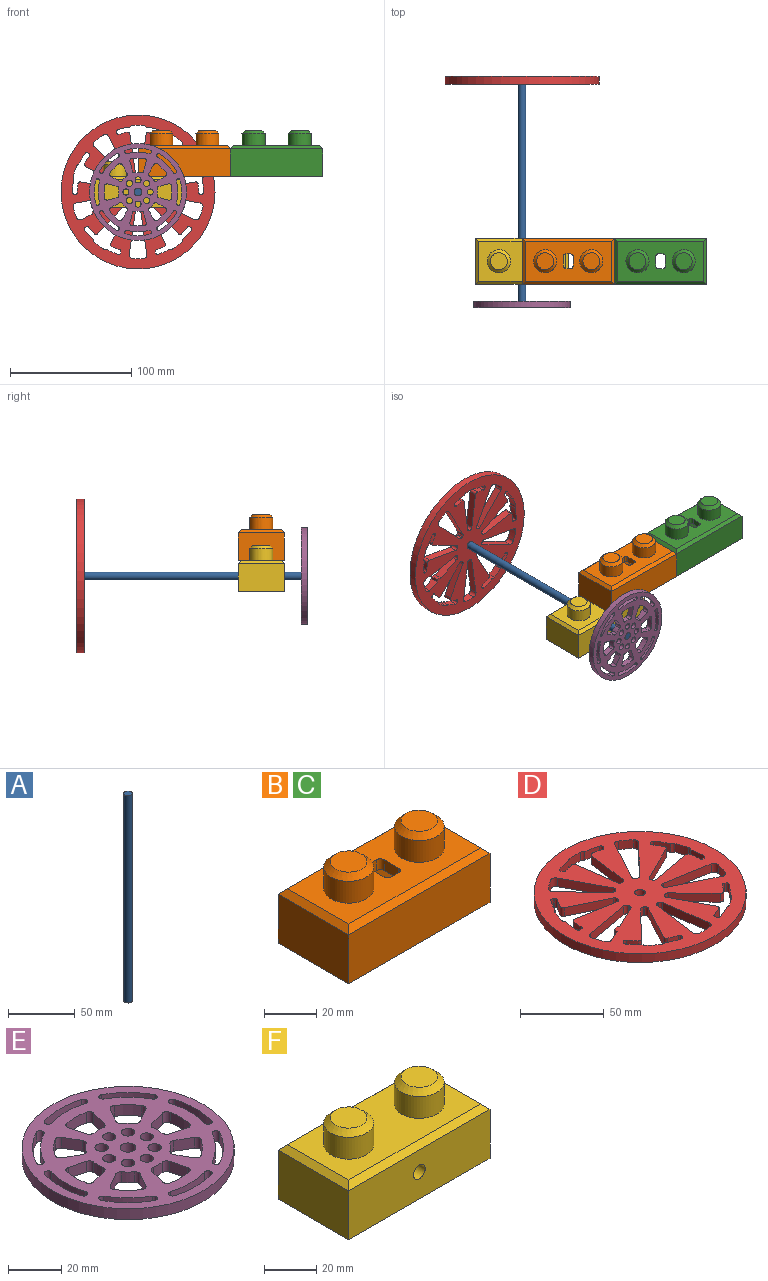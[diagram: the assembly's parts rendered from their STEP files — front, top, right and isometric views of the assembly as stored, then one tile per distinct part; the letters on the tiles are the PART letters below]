
ASSEMBLY  parts=6 mates=5
PART A: 3 faces, bbox 6.4x6.4x190.5 mm
  f0: cylinder r=3.17mm len=190.5mm, axis (0,0,-1), area 3800.3mm2, adj f1,f2
  f1: plane 6.35x6.35mm, normal (0,0,1), area 31.7mm2, adj f0
  f2: plane 6.35x6.35mm, normal (0,0,-1), area 31.7mm2, adj f0
PART B: 33 faces, bbox 76.2x38.1x38.1 mm
  f0: plane 71.12x33.02mm, normal (0,0,1), area 1685.8mm2, adj f7,f9,f13,f14,f15,f16,f25,f26
  f1: plane 66.04x27.94mm, normal (0,0,-1), area 1628.4mm2, adj f19,f20,f21,f22,f23,f24,f25,f26
  f2: plane 76.2x38.1mm, normal (0,0,-1), area 1058.1mm2, adj f3,f4,f5,f6,f19,f20,f21,f22
  f3: plane 76.2x22.86mm, normal (0,1,0), area 1741.9mm2, adj f2,f4,f6,f16
  f4: plane 38.1x22.86mm, normal (-1,0,0), area 871mm2, adj f2,f3,f5,f14
  f5: plane 76.2x22.86mm, normal (0,-1,0), area 1741.9mm2, adj f2,f4,f6,f13
  f6: plane 38.1x22.86mm, normal (1,0,0), area 871mm2, adj f2,f3,f5,f15
  f7: cylinder r=9.53mm len=19.05mm, axis (0,0,-1), area 608mm2, adj f0,f12
  f8: plane 13.97x13.97mm, normal (0,0,1), area 153.3mm2, adj f12
  f9: cylinder r=9.53mm len=19.05mm, axis (0,0,-1), area 608mm2, adj f0,f11
  f10: plane 13.97x13.97mm, normal (0,0,1), area 153.3mm2, adj f11
  f11: cone r=6.99mm half-angle=45deg, axis (0,0,-1), area 186.3mm2, adj f9,f10
  f12: cone r=6.99mm half-angle=45deg, axis (0,0,-1), area 186.3mm2, adj f7,f8
  f13: plane 76.2x2.54mm, normal (0,-0.71,0.71), area 264.6mm2, adj f0,f5,f14,f15
  f14: plane 38.1x2.54mm, normal (-0.71,0,0.71), area 127.7mm2, adj f0,f4,f13,f16
  f15: plane 38.1x2.54mm, normal (0.71,0,0.71), area 127.7mm2, adj f0,f6,f13,f16
  f16: plane 76.2x2.54mm, normal (0,0.71,0.71), area 264.6mm2, adj f0,f3,f14,f15
  f17: plane 8.89x8.89mm, normal (0,0,-1), area 62.1mm2, adj f24
  f18: plane 8.89x8.89mm, normal (0,0,-1), area 62.1mm2, adj f23
  f19: plane 66.04x20.32mm, normal (0,-1,0), area 1341.9mm2, adj f1,f2,f20,f22
  f20: plane 27.94x20.32mm, normal (1,0,0), area 567.7mm2, adj f1,f2,f19,f21
  f21: plane 66.04x20.32mm, normal (0,1,0), area 1341.9mm2, adj f1,f2,f20,f22
  f22: plane 27.94x20.32mm, normal (-1,0,0), area 567.7mm2, adj f1,f2,f19,f21
  f23: cylinder r=4.45mm len=12.7mm, axis (0,0,-1), area 354.7mm2, adj f1,f18
  f24: cylinder r=4.45mm len=12.7mm, axis (0,0,-1), area 354.7mm2, adj f1,f17
  f25: plane 5.08x4mm, normal (0,-1,0), area 20.3mm2, adj f0,f1,f26,f32
  f26: cylinder r=2mm len=5.08mm, axis (0,0,1), area 16mm2, adj f0,f1,f25,f27
  f27: plane 8x5.08mm, normal (1,0,0), area 40.6mm2, adj f0,f1,f26,f28
  f28: cylinder r=2mm len=5.08mm, axis (0,0,1), area 16mm2, adj f0,f1,f27,f29
  f29: plane 5.08x4mm, normal (0,1,0), area 20.3mm2, adj f0,f1,f28,f30
  f30: cylinder r=2mm len=5.08mm, axis (0,0,1), area 16mm2, adj f0,f1,f29,f31
  f31: plane 8x5.08mm, normal (-1,0,0), area 40.6mm2, adj f0,f1,f30,f32
  f32: cylinder r=2mm len=5.08mm, axis (0,0,1), area 16mm2, adj f0,f1,f25,f31
PART C: same geometry as B
PART D: 148 faces, bbox 127x127x6.4 mm
  f0: plane 30.77x6.35mm, normal (-0.99,0.14,0), area 197.3mm2, adj f10,f11,f19,f138
  f1: plane 30.77x6.35mm, normal (0.99,0.14,0), area 197.3mm2, adj f10,f11,f17,f139
  f2: plane 27.93x13.62mm, normal (0.44,-0.9,0), area 197.3mm2, adj f10,f11,f23,f140
  f3: plane 30.6x6.35mm, normal (-0.17,0.98,0), area 197.3mm2, adj f10,f11,f25,f141
  f4: plane 30.6x6.35mm, normal (0.17,0.98,0), area 197.3mm2, adj f10,f11,f29,f142
  f5: plane 27.93x13.62mm, normal (-0.44,-0.9,0), area 197.3mm2, adj f10,f11,f31,f143
  f6: plane 27.44x14.59mm, normal (-0.88,0.47,0), area 197.3mm2, adj f10,f11,f47,f144
  f7: plane 22.35x21.59mm, normal (0.72,-0.69,0), area 197.3mm2, adj f10,f11,f49,f145
  f8: plane 22.35x21.59mm, normal (-0.72,-0.69,0), area 197.3mm2, adj f10,f11,f69,f146
  f9: plane 27.44x14.59mm, normal (0.88,0.47,0), area 197.3mm2, adj f10,f11,f71,f147
  f10: plane 127x127mm, normal (0,0,1), area 8349.2mm2, adj f0,f1,f2,f3,f4,f5,f6,f7
  f11: plane 127x127mm, normal (0,0,-1), area 8349.2mm2, adj f0,f1,f2,f3,f4,f5,f6,f7
  f12: cylinder r=3.17mm len=6.35mm, axis (0,0,-1), area 126.7mm2, adj f10,f11
  f13: cylinder r=63.5mm len=127mm, axis (0,0,-1), area 2533.5mm2, adj f10,f11
  f14: cylinder r=3mm len=6.35mm, axis (0,0,1), area 16.4mm2, adj f10,f11,f15,f136
  f15: cylinder r=55mm len=9mm, axis (0,0,1), area 57.2mm2, adj f10,f11,f14,f16
  f16: cylinder r=3mm len=6.35mm, axis (0,0,1), area 16.4mm2, adj f10,f11,f15,f131
  f17: cylinder r=2mm len=6.35mm, axis (0,0,1), area 18.5mm2, adj f1,f10,f11,f18
  f18: cylinder r=15mm len=6.35mm, axis (0,0,1), area 4.1mm2, adj f10,f11,f17,f19
  f19: cylinder r=2mm len=6.35mm, axis (0,0,1), area 18.5mm2, adj f0,f10,f11,f18
  f20: cylinder r=3mm len=6.35mm, axis (0,0,1), area 16.4mm2, adj f10,f11,f21,f118
  f21: cylinder r=55mm len=8.56mm, axis (0,0,1), area 57.2mm2, adj f10,f11,f20,f22
  f22: cylinder r=3mm len=6.35mm, axis (0,0,1), area 16.4mm2, adj f10,f11,f21,f126
  f23: cylinder r=2mm len=6.35mm, axis (0,0,1), area 18.5mm2, adj f2,f10,f11,f24
  f24: cylinder r=15mm len=6.35mm, axis (0,0,1), area 4.1mm2, adj f10,f11,f23,f25
  f25: cylinder r=2mm len=6.35mm, axis (0,0,1), area 18.5mm2, adj f3,f10,f11,f24
  f26: cylinder r=3mm len=6.35mm, axis (0,0,1), area 16.4mm2, adj f10,f11,f27,f108
  f27: cylinder r=55mm len=8.56mm, axis (0,0,1), area 57.2mm2, adj f10,f11,f26,f28
  f28: cylinder r=3mm len=6.35mm, axis (0,0,1), area 16.4mm2, adj f10,f11,f27,f116
  f29: cylinder r=2mm len=6.35mm, axis (0,0,1), area 18.5mm2, adj f4,f10,f11,f30
  f30: cylinder r=15mm len=6.35mm, axis (0,0,1), area 4.1mm2, adj f10,f11,f29,f31
  f31: cylinder r=2mm len=6.35mm, axis (0,0,1), area 18.5mm2, adj f5,f10,f11,f30
  f32: plane 18.6x9.07mm, normal (-0.44,0.9,0), area 131.4mm2, adj f10,f11,f33,f43
  f33: cylinder r=2mm len=6.35mm, axis (0,0,1), area 18.5mm2, adj f10,f11,f32,f34
  f34: cylinder r=15mm len=6.35mm, axis (0,0,1), area 4.1mm2, adj f10,f11,f33,f35
  f35: cylinder r=2mm len=6.35mm, axis (0,0,1), area 18.5mm2, adj f10,f11,f34,f36
  f36: plane 34.5x6.35mm, normal (0.17,-0.98,0), area 222.4mm2, adj f10,f11,f35,f37
  f37: cylinder r=3mm len=6.35mm, axis (0,0,1), area 31mm2, adj f10,f11,f36,f38
  f38: cylinder r=55mm len=8.56mm, axis (0,0,1), area 57.2mm2, adj f10,f11,f37,f39
  f39: cylinder r=3mm len=6.35mm, axis (0,0,1), area 31mm2, adj f10,f11,f38,f40
  f40: plane 8.79x6.35mm, normal (-0.44,0.9,0), area 62.1mm2, adj f10,f11,f39,f41
  f41: plane 6.35x2.25mm, normal (-1,0.02,0), area 14.3mm2, adj f10,f11,f40,f42
  f42: plane 6.35x3.19mm, normal (-0.29,0.96,0), area 21.2mm2, adj f10,f11,f41,f43
  f43: plane 6.35x1.24mm, normal (0.82,0.58,0), area 9.6mm2, adj f10,f11,f32,f42
  f44: cylinder r=3mm len=6.35mm, axis (0,0,1), area 16.4mm2, adj f10,f11,f45,f98
  f45: cylinder r=55mm len=7.28mm, axis (0,0,1), area 57.2mm2, adj f10,f11,f44,f46
  f46: cylinder r=3mm len=6.35mm, axis (0,0,1), area 16.4mm2, adj f10,f11,f45,f106
  f47: cylinder r=2mm len=6.35mm, axis (0,0,1), area 18.5mm2, adj f6,f10,f11,f48
  f48: cylinder r=15mm len=6.35mm, axis (0,0,1), area 4.1mm2, adj f10,f11,f47,f49
  f49: cylinder r=2mm len=6.35mm, axis (0,0,1), area 18.5mm2, adj f7,f10,f11,f48
  f50: cylinder r=3mm len=6.35mm, axis (0,0,1), area 31mm2, adj f10,f11,f51,f57
  f51: cylinder r=55mm len=9mm, axis (0,0,1), area 57.2mm2, adj f10,f11,f50,f52
  f52: cylinder r=3mm len=6.35mm, axis (0,0,1), area 31mm2, adj f10,f11,f51,f53
  f53: plane 34.69x6.35mm, normal (-0.99,-0.14,0), area 222.4mm2, adj f10,f11,f52,f54
  f54: cylinder r=2mm len=6.35mm, axis (0,0,1), area 18.5mm2, adj f10,f11,f53,f55
  f55: cylinder r=15mm len=6.35mm, axis (0,0,1), area 4.1mm2, adj f10,f11,f54,f56
  f56: cylinder r=2mm len=6.35mm, axis (0,0,1), area 18.5mm2, adj f10,f11,f55,f57
  f57: plane 34.69x6.35mm, normal (0.99,-0.14,0), area 222.4mm2, adj f10,f11,f50,f56
  f58: cylinder r=3mm len=6.35mm, axis (0,0,1), area 31mm2, adj f10,f11,f59,f65
  f59: cylinder r=55mm len=7.28mm, axis (0,0,1), area 57.2mm2, adj f10,f11,f58,f60
  f60: cylinder r=3mm len=6.35mm, axis (0,0,1), area 31mm2, adj f10,f11,f59,f61
  f61: plane 30.93x16.45mm, normal (0.88,-0.47,0), area 222.4mm2, adj f10,f11,f60,f62
  f62: cylinder r=2mm len=6.35mm, axis (0,0,1), area 18.5mm2, adj f10,f11,f61,f63
  f63: cylinder r=15mm len=6.35mm, axis (0,0,1), area 4.1mm2, adj f10,f11,f62,f64
  f64: cylinder r=2mm len=6.35mm, axis (0,0,1), area 18.5mm2, adj f10,f11,f63,f65
  f65: plane 25.2x24.34mm, normal (-0.72,0.69,0), area 222.4mm2, adj f10,f11,f58,f64
  f66: cylinder r=3mm len=6.35mm, axis (0,0,1), area 16.4mm2, adj f10,f11,f67,f88
  f67: cylinder r=55mm len=7.28mm, axis (0,0,1), area 57.2mm2, adj f10,f11,f66,f68
  f68: cylinder r=3mm len=6.35mm, axis (0,0,1), area 16.4mm2, adj f10,f11,f67,f96
  f69: cylinder r=2mm len=6.35mm, axis (0,0,1), area 18.5mm2, adj f8,f10,f11,f70
  f70: cylinder r=15mm len=6.35mm, axis (0,0,1), area 4.1mm2, adj f10,f11,f69,f71
  f71: cylinder r=2mm len=6.35mm, axis (0,0,1), area 18.5mm2, adj f9,f10,f11,f70
  f72: cylinder r=3mm len=6.35mm, axis (0,0,1), area 31mm2, adj f10,f11,f73,f79
  f73: cylinder r=55mm len=8.56mm, axis (0,0,1), area 57.2mm2, adj f10,f11,f72,f74
  f74: cylinder r=3mm len=6.35mm, axis (0,0,1), area 31mm2, adj f10,f11,f73,f75
  f75: plane 34.5x6.35mm, normal (-0.17,-0.98,0), area 222.4mm2, adj f10,f11,f74,f76
  f76: cylinder r=2mm len=6.35mm, axis (0,0,1), area 18.5mm2, adj f10,f11,f75,f77
  f77: cylinder r=15mm len=6.35mm, axis (0,0,1), area 4.1mm2, adj f10,f11,f76,f78
  f78: cylinder r=2mm len=6.35mm, axis (0,0,1), area 18.5mm2, adj f10,f11,f77,f79
  f79: plane 31.49x15.36mm, normal (0.44,0.9,0), area 222.4mm2, adj f10,f11,f72,f78
  f80: cylinder r=3mm len=6.35mm, axis (0,0,1), area 31mm2, adj f10,f11,f81,f87
  f81: cylinder r=55mm len=7.28mm, axis (0,0,1), area 57.2mm2, adj f10,f11,f80,f82
  f82: cylinder r=3mm len=6.35mm, axis (0,0,1), area 31mm2, adj f10,f11,f81,f83
  f83: plane 25.2x24.34mm, normal (0.72,0.69,0), area 222.4mm2, adj f10,f11,f82,f84
  f84: cylinder r=2mm len=6.35mm, axis (0,0,1), area 18.5mm2, adj f10,f11,f83,f85
  f85: cylinder r=15mm len=6.35mm, axis (0,0,1), area 4.1mm2, adj f10,f11,f84,f86
  f86: cylinder r=2mm len=6.35mm, axis (0,0,1), area 18.5mm2, adj f10,f11,f85,f87
  f87: plane 30.93x16.45mm, normal (-0.88,-0.47,0), area 222.4mm2, adj f10,f11,f80,f86
  f88: cylinder r=54mm len=9.73mm, axis (0,0,1), area 67.3mm2, adj f10,f11,f66,f89
  f89: cylinder r=1.5mm len=6.35mm, axis (0,0,1), area 15.2mm2, adj f10,f11,f88,f90
  f90: plane 6.35x0.96mm, normal (0.96,0.28,0), area 6.4mm2, adj f10,f11,f89,f92
  f91: cylinder r=50mm len=6.44mm, axis (0,0,1), area 44mm2, adj f10,f11,f92,f147
  f92: cylinder r=1.5mm len=6.35mm, axis (0,0,1), area 14.7mm2, adj f10,f11,f90,f91
  f93: cylinder r=1.5mm len=6.35mm, axis (0,0,1), area 15.2mm2, adj f10,f11,f94,f96
  f94: plane 6.35x0.83mm, normal (-0.56,-0.83,0), area 6.4mm2, adj f10,f11,f93,f95
  f95: cylinder r=1.5mm len=6.35mm, axis (0,0,1), area 14.7mm2, adj f10,f11,f94,f97
  f96: cylinder r=54mm len=7.96mm, axis (0,0,1), area 67.3mm2, adj f10,f11,f68,f93
  f97: cylinder r=50mm len=6.35mm, axis (0,0,1), area 44mm2, adj f10,f11,f95,f146
  f98: cylinder r=54mm len=7.96mm, axis (0,0,1), area 67.3mm2, adj f10,f11,f44,f99
  f99: cylinder r=1.5mm len=6.35mm, axis (0,0,1), area 15.2mm2, adj f10,f11,f98,f100
  f100: plane 6.35x0.83mm, normal (0.56,-0.83,0), area 6.4mm2, adj f10,f11,f99,f102
  f101: cylinder r=50mm len=6.35mm, axis (0,0,1), area 44mm2, adj f10,f11,f102,f145
  f102: cylinder r=1.5mm len=6.35mm, axis (0,0,1), area 14.7mm2, adj f10,f11,f100,f101
  f103: cylinder r=1.5mm len=6.35mm, axis (0,0,1), area 15.2mm2, adj f10,f11,f104,f106
  f104: plane 6.35x0.96mm, normal (-0.96,0.28,0), area 6.4mm2, adj f10,f11,f103,f105
  f105: cylinder r=1.5mm len=6.35mm, axis (0,0,1), area 14.7mm2, adj f10,f11,f104,f107
  f106: cylinder r=54mm len=9.73mm, axis (0,0,1), area 67.3mm2, adj f10,f11,f46,f103
  f107: cylinder r=50mm len=6.44mm, axis (0,0,1), area 44mm2, adj f10,f11,f105,f144
  f108: cylinder r=54mm len=9.1mm, axis (0,0,1), area 67.3mm2, adj f10,f11,f26,f109
  f109: cylinder r=1.5mm len=6.35mm, axis (0,0,1), area 15.2mm2, adj f10,f11,f108,f110
  f110: plane 6.35x0.79mm, normal (-0.62,-0.79,0), area 6.4mm2, adj f10,f11,f109,f112
  f111: cylinder r=50mm len=6.35mm, axis (0,0,1), area 44mm2, adj f10,f11,f112,f143
  f112: cylinder r=1.5mm len=6.35mm, axis (0,0,1), area 14.7mm2, adj f10,f11,f110,f111
  f113: cylinder r=1.5mm len=6.35mm, axis (0,0,1), area 15.2mm2, adj f10,f11,f114,f116
  f114: plane 6.35x1mm, normal (-0.03,1,0), area 6.4mm2, adj f10,f11,f113,f115
  f115: cylinder r=1.5mm len=6.35mm, axis (0,0,1), area 14.7mm2, adj f10,f11,f114,f117
  f116: cylinder r=54mm len=10.54mm, axis (0,0,1), area 67.3mm2, adj f10,f11,f28,f113
  f117: cylinder r=50mm len=6.91mm, axis (0,0,1), area 44mm2, adj f10,f11,f115,f142
  f118: cylinder r=54mm len=10.54mm, axis (0,0,1), area 67.3mm2, adj f10,f11,f20,f119
  f119: cylinder r=1.5mm len=6.35mm, axis (0,0,1), area 15.2mm2, adj f10,f11,f118,f120
  f120: plane 6.35x1mm, normal (0.03,1,0), area 6.4mm2, adj f10,f11,f119,f122
  f121: cylinder r=50mm len=6.91mm, axis (0,0,1), area 44mm2, adj f10,f11,f122,f141
  f122: cylinder r=1.5mm len=6.35mm, axis (0,0,1), area 14.7mm2, adj f10,f11,f120,f121
  f123: cylinder r=1.5mm len=6.35mm, axis (0,0,1), area 15.2mm2, adj f10,f11,f124,f126
  f124: plane 6.35x0.79mm, normal (0.62,-0.79,0), area 6.4mm2, adj f10,f11,f123,f125
  f125: cylinder r=1.5mm len=6.35mm, axis (0,0,1), area 14.7mm2, adj f10,f11,f124,f127
  f126: cylinder r=54mm len=9.1mm, axis (0,0,1), area 67.3mm2, adj f10,f11,f22,f123
  f127: cylinder r=50mm len=6.35mm, axis (0,0,1), area 44mm2, adj f10,f11,f125,f140
  f128: cylinder r=50mm len=6.71mm, axis (0,0,1), area 44mm2, adj f10,f11,f129,f139
  f129: cylinder r=1.5mm len=6.35mm, axis (0,0,1), area 14.7mm2, adj f10,f11,f128,f130
  f130: plane 6.35x0.94mm, normal (0.94,0.34,0), area 6.4mm2, adj f10,f11,f129,f132
  f131: cylinder r=54mm len=10.33mm, axis (0,0,1), area 67.3mm2, adj f10,f11,f16,f132
  f132: cylinder r=1.5mm len=6.35mm, axis (0,0,1), area 15.2mm2, adj f10,f11,f130,f131
  f133: cylinder r=1.5mm len=6.35mm, axis (0,0,1), area 14.7mm2, adj f10,f11,f134,f137
  f134: plane 6.35x0.94mm, normal (-0.94,0.34,0), area 6.4mm2, adj f10,f11,f133,f135
  f135: cylinder r=1.5mm len=6.35mm, axis (0,0,1), area 15.2mm2, adj f10,f11,f134,f136
  f136: cylinder r=54mm len=10.33mm, axis (0,0,1), area 67.3mm2, adj f10,f11,f14,f135
  f137: cylinder r=50mm len=6.71mm, axis (0,0,1), area 44mm2, adj f10,f11,f133,f138
  f138: cylinder r=2mm len=6.35mm, axis (0,0,1), area 20.5mm2, adj f0,f10,f11,f137
  f139: cylinder r=2mm len=6.35mm, axis (0,0,1), area 20.5mm2, adj f1,f10,f11,f128
  f140: cylinder r=2mm len=6.35mm, axis (0,0,1), area 20.5mm2, adj f2,f10,f11,f127
  f141: cylinder r=2mm len=6.35mm, axis (0,0,1), area 20.5mm2, adj f3,f10,f11,f121
  f142: cylinder r=2mm len=6.35mm, axis (0,0,1), area 20.5mm2, adj f4,f10,f11,f117
  f143: cylinder r=2mm len=6.35mm, axis (0,0,1), area 20.5mm2, adj f5,f10,f11,f111
  f144: cylinder r=2mm len=6.35mm, axis (0,0,1), area 20.5mm2, adj f6,f10,f11,f107
  f145: cylinder r=2mm len=6.35mm, axis (0,0,1), area 20.5mm2, adj f7,f10,f11,f101
  f146: cylinder r=2mm len=6.35mm, axis (0,0,1), area 20.5mm2, adj f8,f10,f11,f97
  f147: cylinder r=2mm len=6.35mm, axis (0,0,1), area 20.5mm2, adj f9,f10,f11,f91
PART E: 108 faces, bbox 80x80x5 mm
  f0: plane 80x80mm, normal (0,0,1), area 3243.3mm2, adj f2,f3,f4,f5,f6,f7,f8,f9
  f1: plane 80x80mm, normal (0,0,-1), area 3243.3mm2, adj f2,f3,f4,f5,f6,f7,f8,f9
  f2: cylinder r=3mm len=6mm, axis (0,0,-1), area 94.2mm2, adj f0,f1
  f3: cylinder r=40mm len=80mm, axis (0,0,-1), area 1256.6mm2, adj f0,f1
  f4: cylinder r=2.5mm len=5mm, axis (0,0,1), area 78.5mm2, adj f0,f1
  f5: cylinder r=2.5mm len=5mm, axis (0,0,1), area 78.5mm2, adj f0,f1
  f6: cylinder r=2.5mm len=5mm, axis (0,0,1), area 78.5mm2, adj f0,f1
  f7: cylinder r=2.5mm len=5mm, axis (0,0,1), area 78.5mm2, adj f0,f1
  f8: cylinder r=2.5mm len=5mm, axis (0,0,1), area 78.5mm2, adj f0,f1
  f9: cylinder r=2.5mm len=5mm, axis (0,0,1), area 78.5mm2, adj f0,f1
  f10: cylinder r=2.5mm len=5mm, axis (0,0,1), area 78.5mm2, adj f0,f1
  f11: cylinder r=2.5mm len=5mm, axis (0,0,1), area 78.5mm2, adj f0,f1
  f12: cylinder r=33mm len=18.19mm, axis (0,0,1), area 92.2mm2, adj f0,f1,f13,f15
  f13: cylinder r=1.5mm len=5mm, axis (0,0,1), area 23.6mm2, adj f0,f1,f12,f14
  f14: cylinder r=36mm len=19.85mm, axis (0,0,1), area 100.5mm2, adj f0,f1,f13,f15
  f15: cylinder r=1.5mm len=5mm, axis (0,0,1), area 23.6mm2, adj f0,f1,f12,f14
  f16: cylinder r=1.5mm len=5mm, axis (0,0,1), area 23.6mm2, adj f0,f1,f17,f19
  f17: cylinder r=36mm len=14.03mm, axis (0,0,1), area 100.5mm2, adj f0,f1,f16,f18
  f18: cylinder r=1.5mm len=5mm, axis (0,0,1), area 23.6mm2, adj f0,f1,f17,f19
  f19: cylinder r=33mm len=12.86mm, axis (0,0,1), area 92.2mm2, adj f0,f1,f16,f18
  f20: cylinder r=1.5mm len=5mm, axis (0,0,1), area 23.6mm2, adj f0,f1,f21,f23
  f21: cylinder r=36mm len=19.85mm, axis (0,0,1), area 100.5mm2, adj f0,f1,f20,f22
  f22: cylinder r=1.5mm len=5mm, axis (0,0,1), area 23.6mm2, adj f0,f1,f21,f23
  f23: cylinder r=33mm len=18.19mm, axis (0,0,1), area 92.2mm2, adj f0,f1,f20,f22
  f24: cylinder r=1.5mm len=5mm, axis (0,0,1), area 23.6mm2, adj f0,f1,f25,f27
  f25: cylinder r=36mm len=14.03mm, axis (0,0,1), area 100.5mm2, adj f0,f1,f24,f26
  f26: cylinder r=1.5mm len=5mm, axis (0,0,1), area 23.6mm2, adj f0,f1,f25,f27
  f27: cylinder r=33mm len=12.86mm, axis (0,0,1), area 92.2mm2, adj f0,f1,f24,f26
  f28: cylinder r=1.5mm len=5mm, axis (0,0,1), area 23.6mm2, adj f0,f1,f29,f31
  f29: cylinder r=36mm len=19.85mm, axis (0,0,1), area 100.5mm2, adj f0,f1,f28,f30
  f30: cylinder r=1.5mm len=5mm, axis (0,0,1), area 23.6mm2, adj f0,f1,f29,f31
  f31: cylinder r=33mm len=18.19mm, axis (0,0,1), area 92.2mm2, adj f0,f1,f28,f30
  f32: cylinder r=1.5mm len=5mm, axis (0,0,1), area 23.6mm2, adj f0,f1,f33,f35
  f33: cylinder r=36mm len=14.03mm, axis (0,0,1), area 100.5mm2, adj f0,f1,f32,f34
  f34: cylinder r=1.5mm len=5mm, axis (0,0,1), area 23.6mm2, adj f0,f1,f33,f35
  f35: cylinder r=33mm len=12.86mm, axis (0,0,1), area 92.2mm2, adj f0,f1,f32,f34
  f36: cylinder r=1.5mm len=5mm, axis (0,0,1), area 23.6mm2, adj f0,f1,f37,f39
  f37: cylinder r=36mm len=19.85mm, axis (0,0,1), area 100.5mm2, adj f0,f1,f36,f38
  f38: cylinder r=1.5mm len=5mm, axis (0,0,1), area 23.6mm2, adj f0,f1,f37,f39
  f39: cylinder r=33mm len=18.19mm, axis (0,0,1), area 92.2mm2, adj f0,f1,f36,f38
  f40: cylinder r=1.5mm len=5mm, axis (0,0,1), area 23.6mm2, adj f0,f1,f41,f43
  f41: cylinder r=36mm len=14.03mm, axis (0,0,1), area 100.5mm2, adj f0,f1,f40,f42
  f42: cylinder r=1.5mm len=5mm, axis (0,0,1), area 23.6mm2, adj f0,f1,f41,f43
  f43: cylinder r=33mm len=12.86mm, axis (0,0,1), area 92.2mm2, adj f0,f1,f40,f42
  f44: cylinder r=28mm len=10.29mm, axis (0,0,1), area 51.7mm2, adj f0,f1,f45,f51
  f45: cylinder r=2mm len=5mm, axis (0,0,1), area 16.5mm2, adj f0,f1,f44,f46
  f46: plane 7.76x5mm, normal (-0.26,0.97,0), area 40.2mm2, adj f0,f1,f45,f47
  f47: cylinder r=2mm len=5mm, axis (0,0,1), area 14.6mm2, adj f0,f1,f46,f48
  f48: cylinder r=16mm len=5mm, axis (0,0,1), area 24.1mm2, adj f0,f1,f47,f49
  f49: cylinder r=2mm len=5mm, axis (0,0,1), area 14.6mm2, adj f0,f1,f48,f50
  f50: plane 7.76x5mm, normal (-0.26,-0.97,0), area 40.2mm2, adj f0,f1,f49,f51
  f51: cylinder r=2mm len=5mm, axis (0,0,1), area 16.5mm2, adj f0,f1,f44,f50
  f52: cylinder r=2mm len=5mm, axis (0,0,1), area 16.5mm2, adj f0,f1,f53,f59
  f53: cylinder r=28mm len=7.28mm, axis (0,0,1), area 51.7mm2, adj f0,f1,f52,f54
  f54: cylinder r=2mm len=5mm, axis (0,0,1), area 16.5mm2, adj f0,f1,f53,f55
  f55: plane 6.96x5mm, normal (-0.87,0.5,0), area 40.2mm2, adj f0,f1,f54,f56
  f56: cylinder r=2mm len=5mm, axis (0,0,1), area 14.6mm2, adj f0,f1,f55,f57
  f57: cylinder r=16mm len=5mm, axis (0,0,1), area 24.1mm2, adj f0,f1,f56,f58
  f58: cylinder r=2mm len=5mm, axis (0,0,1), area 14.6mm2, adj f0,f1,f57,f59
  f59: plane 6.96x5mm, normal (0.5,-0.87,0), area 40.2mm2, adj f0,f1,f52,f58
  f60: cylinder r=2mm len=5mm, axis (0,0,1), area 16.5mm2, adj f0,f1,f61,f67
  f61: cylinder r=28mm len=10.29mm, axis (0,0,1), area 51.7mm2, adj f0,f1,f60,f62
  f62: cylinder r=2mm len=5mm, axis (0,0,1), area 16.5mm2, adj f0,f1,f61,f63
  f63: plane 7.76x5mm, normal (-0.97,-0.26,0), area 40.2mm2, adj f0,f1,f62,f64
  f64: cylinder r=2mm len=5mm, axis (0,0,1), area 14.6mm2, adj f0,f1,f63,f65
  f65: cylinder r=16mm len=5mm, axis (0,0,1), area 24.1mm2, adj f0,f1,f64,f66
  f66: cylinder r=2mm len=5mm, axis (0,0,1), area 14.6mm2, adj f0,f1,f65,f67
  f67: plane 7.76x5mm, normal (0.97,-0.26,0), area 40.2mm2, adj f0,f1,f60,f66
  f68: cylinder r=2mm len=5mm, axis (0,0,1), area 16.5mm2, adj f0,f1,f69,f75
  f69: cylinder r=28mm len=7.28mm, axis (0,0,1), area 51.7mm2, adj f0,f1,f68,f70
  f70: cylinder r=2mm len=5mm, axis (0,0,1), area 16.5mm2, adj f0,f1,f69,f71
  f71: plane 6.96x5mm, normal (-0.5,-0.87,0), area 40.2mm2, adj f0,f1,f70,f72
  f72: cylinder r=2mm len=5mm, axis (0,0,1), area 14.6mm2, adj f0,f1,f71,f73
  f73: cylinder r=16mm len=5mm, axis (0,0,1), area 24.1mm2, adj f0,f1,f72,f74
  f74: cylinder r=2mm len=5mm, axis (0,0,1), area 14.6mm2, adj f0,f1,f73,f75
  f75: plane 6.96x5mm, normal (0.87,0.5,0), area 40.2mm2, adj f0,f1,f68,f74
  f76: cylinder r=2mm len=5mm, axis (0,0,1), area 16.5mm2, adj f0,f1,f77,f83
  f77: cylinder r=28mm len=10.29mm, axis (0,0,1), area 51.7mm2, adj f0,f1,f76,f78
  f78: cylinder r=2mm len=5mm, axis (0,0,1), area 16.5mm2, adj f0,f1,f77,f79
  f79: plane 7.76x5mm, normal (0.26,-0.97,0), area 40.2mm2, adj f0,f1,f78,f80
  f80: cylinder r=2mm len=5mm, axis (0,0,1), area 14.6mm2, adj f0,f1,f79,f81
  f81: cylinder r=16mm len=5mm, axis (0,0,1), area 24.1mm2, adj f0,f1,f80,f82
  f82: cylinder r=2mm len=5mm, axis (0,0,1), area 14.6mm2, adj f0,f1,f81,f83
  f83: plane 7.76x5mm, normal (0.26,0.97,0), area 40.2mm2, adj f0,f1,f76,f82
  f84: cylinder r=2mm len=5mm, axis (0,0,1), area 16.5mm2, adj f0,f1,f85,f91
  f85: cylinder r=28mm len=7.28mm, axis (0,0,1), area 51.7mm2, adj f0,f1,f84,f86
  f86: cylinder r=2mm len=5mm, axis (0,0,1), area 16.5mm2, adj f0,f1,f85,f87
  f87: plane 6.96x5mm, normal (0.87,-0.5,0), area 40.2mm2, adj f0,f1,f86,f88
  f88: cylinder r=2mm len=5mm, axis (0,0,1), area 14.6mm2, adj f0,f1,f87,f89
  f89: cylinder r=16mm len=5mm, axis (0,0,1), area 24.1mm2, adj f0,f1,f88,f90
  f90: cylinder r=2mm len=5mm, axis (0,0,1), area 14.6mm2, adj f0,f1,f89,f91
  f91: plane 6.96x5mm, normal (-0.5,0.87,0), area 40.2mm2, adj f0,f1,f84,f90
  f92: cylinder r=2mm len=5mm, axis (0,0,1), area 16.5mm2, adj f0,f1,f93,f99
  f93: cylinder r=28mm len=10.29mm, axis (0,0,1), area 51.7mm2, adj f0,f1,f92,f94
  f94: cylinder r=2mm len=5mm, axis (0,0,1), area 16.5mm2, adj f0,f1,f93,f95
  f95: plane 7.76x5mm, normal (0.97,0.26,0), area 40.2mm2, adj f0,f1,f94,f96
  f96: cylinder r=2mm len=5mm, axis (0,0,1), area 14.6mm2, adj f0,f1,f95,f97
  f97: cylinder r=16mm len=5mm, axis (0,0,1), area 24.1mm2, adj f0,f1,f96,f98
  f98: cylinder r=2mm len=5mm, axis (0,0,1), area 14.6mm2, adj f0,f1,f97,f99
  f99: plane 7.76x5mm, normal (-0.97,0.26,0), area 40.2mm2, adj f0,f1,f92,f98
  f100: cylinder r=2mm len=5mm, axis (0,0,1), area 16.5mm2, adj f0,f1,f101,f107
  f101: cylinder r=28mm len=7.28mm, axis (0,0,1), area 51.7mm2, adj f0,f1,f100,f102
  f102: cylinder r=2mm len=5mm, axis (0,0,1), area 16.5mm2, adj f0,f1,f101,f103
  f103: plane 6.96x5mm, normal (0.5,0.87,0), area 40.2mm2, adj f0,f1,f102,f104
  f104: cylinder r=2mm len=5mm, axis (0,0,1), area 14.6mm2, adj f0,f1,f103,f105
  f105: cylinder r=16mm len=5mm, axis (0,0,1), area 24.1mm2, adj f0,f1,f104,f106
  f106: cylinder r=2mm len=5mm, axis (0,0,1), area 14.6mm2, adj f0,f1,f105,f107
  f107: plane 6.96x5mm, normal (-0.87,-0.5,0), area 40.2mm2, adj f0,f1,f100,f106
PART F: 27 faces, bbox 76.2x38.1x38.1 mm
  f0: plane 76.2x38.1mm, normal (0,0,-1), area 1058.1mm2, adj f1,f2,f3,f4,f19,f20,f21,f22
  f1: plane 76.2x22.86mm, normal (0,1,0), area 1710.3mm2, adj f0,f2,f4,f15,f26
  f2: plane 38.1x22.86mm, normal (-1,0,0), area 871mm2, adj f0,f1,f3,f13
  f3: plane 76.2x22.86mm, normal (0,-1,0), area 1710.3mm2, adj f0,f2,f4,f12,f25
  f4: plane 38.1x22.86mm, normal (1,0,0), area 871mm2, adj f0,f1,f3,f14
  f5: plane 71.12x33.02mm, normal (0,0,1), area 1778.3mm2, adj f6,f8,f12,f13,f14,f15
  f6: cylinder r=9.53mm len=19.05mm, axis (0,0,-1), area 608mm2, adj f5,f11
  f7: plane 13.97x13.97mm, normal (0,0,1), area 153.3mm2, adj f11
  f8: cylinder r=9.53mm len=19.05mm, axis (0,0,-1), area 608mm2, adj f5,f10
  f9: plane 13.97x13.97mm, normal (0,0,1), area 153.3mm2, adj f10
  f10: cone r=6.99mm half-angle=45deg, axis (0,0,-1), area 186.3mm2, adj f8,f9
  f11: cone r=6.99mm half-angle=45deg, axis (0,0,-1), area 186.3mm2, adj f6,f7
  f12: plane 76.2x2.54mm, normal (0,-0.71,0.71), area 264.6mm2, adj f3,f5,f13,f14
  f13: plane 38.1x2.54mm, normal (-0.71,0,0.71), area 127.7mm2, adj f2,f5,f12,f15
  f14: plane 38.1x2.54mm, normal (0.71,0,0.71), area 127.7mm2, adj f4,f5,f12,f15
  f15: plane 76.2x2.54mm, normal (0,0.71,0.71), area 264.6mm2, adj f1,f5,f13,f14
  f16: plane 8.89x8.89mm, normal (0,0,-1), area 62.1mm2, adj f24
  f17: plane 8.89x8.89mm, normal (0,0,-1), area 62.1mm2, adj f23
  f18: plane 66.04x27.94mm, normal (0,0,-1), area 1721mm2, adj f19,f20,f21,f22,f23,f24
  f19: plane 66.04x20.32mm, normal (0,-1,0), area 1310.3mm2, adj f0,f18,f20,f22,f26
  f20: plane 27.94x20.32mm, normal (1,0,0), area 567.7mm2, adj f0,f18,f19,f21
  f21: plane 66.04x20.32mm, normal (0,1,0), area 1310.3mm2, adj f0,f18,f20,f22,f25
  f22: plane 27.94x20.32mm, normal (-1,0,0), area 567.7mm2, adj f0,f18,f19,f21
  f23: cylinder r=4.45mm len=12.7mm, axis (0,0,-1), area 354.7mm2, adj f17,f18
  f24: cylinder r=4.45mm len=12.7mm, axis (0,0,-1), area 354.7mm2, adj f16,f18
  f25: cylinder r=3.17mm len=6.35mm, axis (0,-1,0), area 101.3mm2, adj f3,f21
  f26: cylinder r=3.17mm len=6.35mm, axis (0,-1,0), area 101.3mm2, adj f1,f19
PLACE A rot(axis=(1,0,0),90deg) t=(38.1,171.45,12.7)mm
PLACE B t=(76.2,19.05,25.4)mm
PLACE C t=(152.4,19.05,25.4)mm
PLACE D rot(axis=(1,0,0),90deg) t=(38.1,171.45,12.7)mm
PLACE E rot(axis=(1,0,0),90deg) t=(38.1,-14.05,12.7)mm
PLACE F t=(38.1,19.05,0)mm
MATE fastened A.f0 <-> D.f38  axis (0,1,0) through (38.1,171.45,12.7)mm
MATE fastened F.f5 <-> B.f2  axis (0,0,1) through (38.1,19.05,25.4)mm
MATE fastened F.f25 <-> A.f0  axis (0,-1,0) through (38.1,0,12.7)mm
MATE revolute A.f0 <-> E.f2  axis (0,-1,0) through (38.1,-19.05,12.7)mm
MATE fastened C.f4 <-> B.f6  axis (-1,0,0) through (114.3,19.05,36.83)mm
